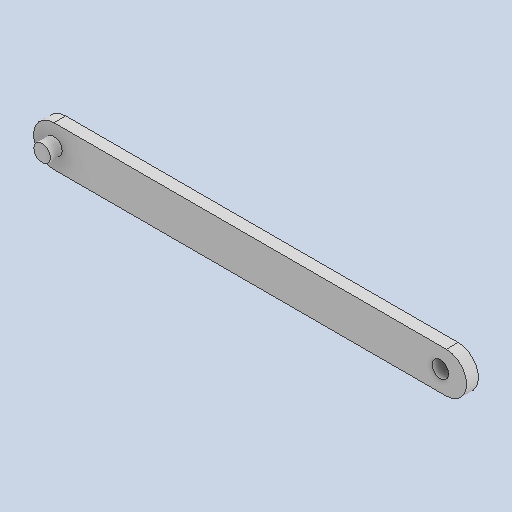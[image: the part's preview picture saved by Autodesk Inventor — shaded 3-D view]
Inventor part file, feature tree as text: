
AUTODESK INVENTOR PART (.ipt)
format: ipt  version: 2024.1 (Build 281209000, 209)  size: 108,032 bytes
history: native  units: mm
features: extrude x5, sketch x5
ambient origin geometry x8: Origin, YZ Plane, XZ Plane, XY Plane, X Axis, Y Axis, Z Axis, Center Point
bodies: Solid1 (feature_tree)
feature tree (10):
  extrude  "Extrusion1"  Depth=3.0mm TaperAngle=0.0deg
  extrude  "Extrusion2"  Depth=3.0mm TaperAngle=0.0deg
  extrude  "Extrusion3"  Depth=3.0mm TaperAngle=0.0deg
  extrude  "Extrusion4"  Depth=10.0mm TaperAngle=0.0deg
  extrude  "Extrusion5"  Depth=10.0mm TaperAngle=0.0deg
  sketch  "Sketch1"  dims[d0=100.0mm d1=3.0mm d2=0.0mm]
  sketch  "Sketch2"  dims[d3=4.25mm d4=3.0mm d5=6.0mm d6=0.0mm d7=0.0mm]
  sketch  "Sketch3"  dims[d8=4.25mm d9=3.0mm d10=0.0mm]
  sketch  "Sketch4"  dims[d11=4.25mm d12=10.0mm d13=0.0mm]
  sketch  "Sketch5"  dims[d14=4.25mm d15=10.0mm d16=0.0mm]
